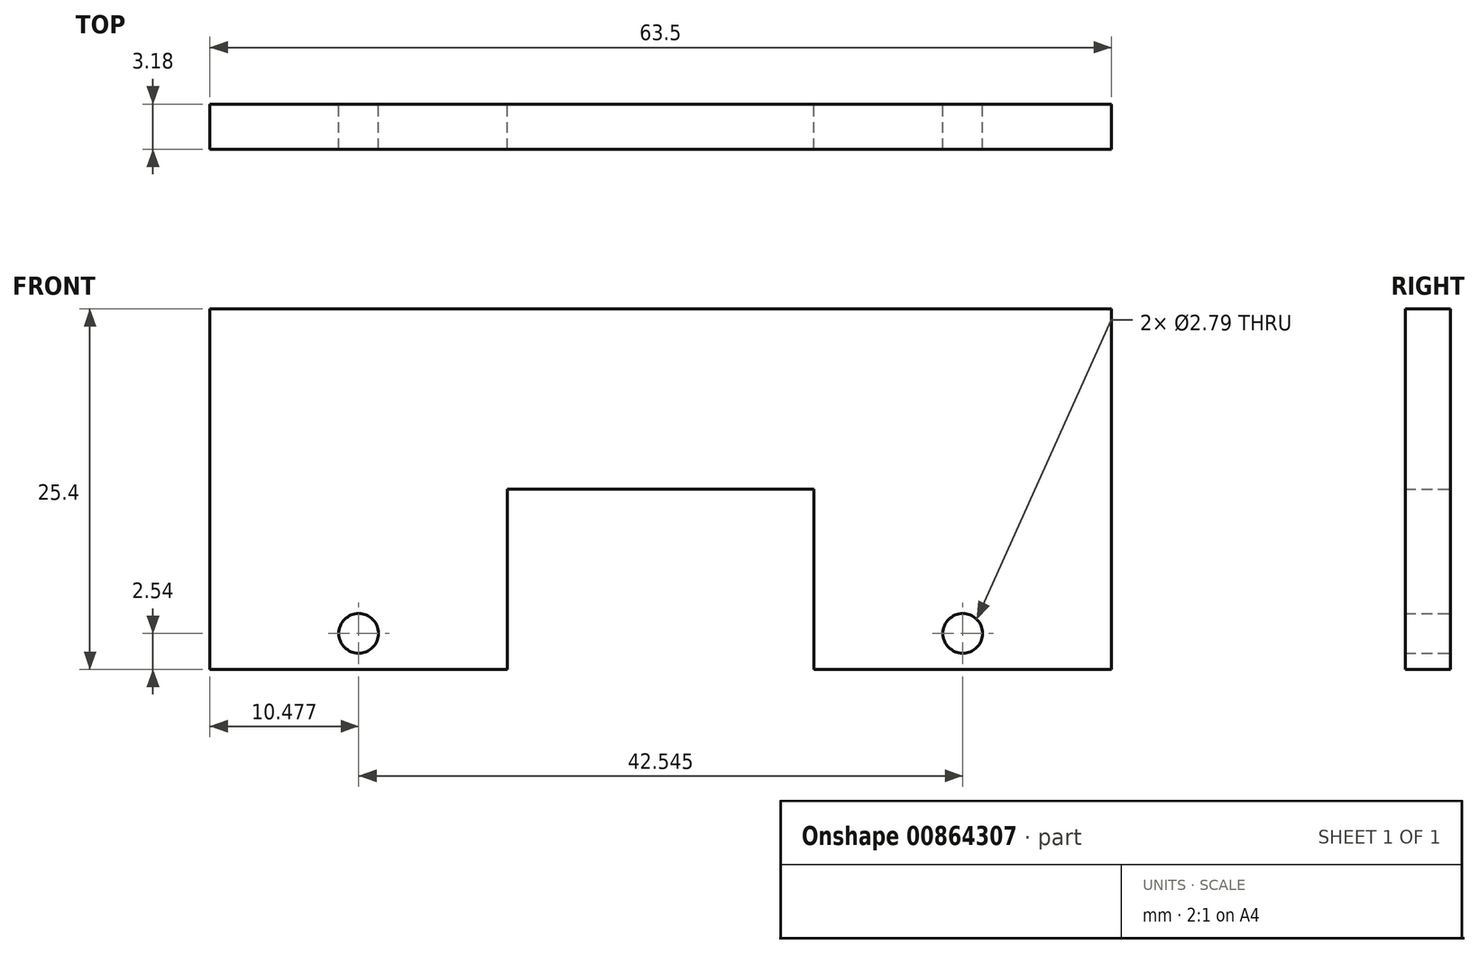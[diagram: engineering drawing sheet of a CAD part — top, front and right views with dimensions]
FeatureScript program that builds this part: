
annotation { "Feature Type Name" : "Feature", "Feature Type Description" : "" }
export const myFeature = defineFeature(function(context is Context, id is Id, definition is map)
    precondition{}
    {
        {
            var Q0;
            Q0=qCreatedBy(makeId("Front.planeOp"),FACE);
            var sketch = newSketch(context, id + "F0", { "sketchPlane" : qUnion([Q0])});
            skLineSegment(sketch, "E0.bottom", {"start": v(31.75, 25.4) * mm, "end": v(-31.75, 25.4) * mm});
            skLineSegment(sketch, "E0.top", {"start": v(31.75, -25.4) * mm, "end": v(-31.75, -25.4) * mm});
            skLineSegment(sketch, "E0.left", {"start": v(31.75, 25.4) * mm, "end": v(31.75, -25.4) * mm});
            skLineSegment(sketch, "E0.right", {"start": v(-31.75, 25.4) * mm, "end": v(-31.75, -25.4) * mm});
            skPoint(sketch, "E0.middle", {"position": v(0, 0) * mm});
            skLineSegment(sketch, "E1", {"start": v(-31.75, 0) * mm, "end": v(31.75, 0) * mm});
            skLineSegment(sketch, "E2.bottom", {"start": v(10.8, 12.7) * mm, "end": v(-10.8, 12.7) * mm});
            skLineSegment(sketch, "E2.top", {"start": v(10.8, -12.7) * mm, "end": v(-10.8, -12.7) * mm});
            skLineSegment(sketch, "E2.left", {"start": v(10.8, 12.7) * mm, "end": v(10.8, -12.7) * mm});
            skLineSegment(sketch, "E2.right", {"start": v(-10.8, 12.7) * mm, "end": v(-10.8, -12.7) * mm});
            skLineSegment(sketch, "E3", {"start": v(10.8, 0) * mm, "end": v(31.75, 0) * mm});
            skLineSegment(sketch, "E4", {"start": v(-10.8, 0) * mm, "end": v(-31.75, 0) * mm});
            skCircle(sketch, "E5", {"center": v(21.27, 2.54) * mm, "radius": 1.4 * mm});
            skPoint(sketch, "E5.centerSnap0", {"position": v(21.27, 0) * mm});
            skCircle(sketch, "E6", {"center": v(-21.27, 2.54) * mm, "radius": 1.4 * mm});
            skPoint(sketch, "E6.centerSnap0", {"position": v(-21.27, 0) * mm});
            skSolve(sketch);
        }
        {
            var Q0;
            {var subQ1=sQuery(id+"F0.wireOp",EDGE,"E0.bottom");Q0=makeQuery(id+"F0.imprint","IMPRINT",FACE,{"disambiguationData":[TD([[makeQuery(id+"F0.imprint","IMPRINT",EDGE,{"derivedFrom":subQ1}),1.0]])]});}
            extrude(context, id + "F1", {"entities" : qUnion([Q0]), "depth" : 3.17 * mm, "offsetDistance" : 25.4 * mm});
        }
    });
